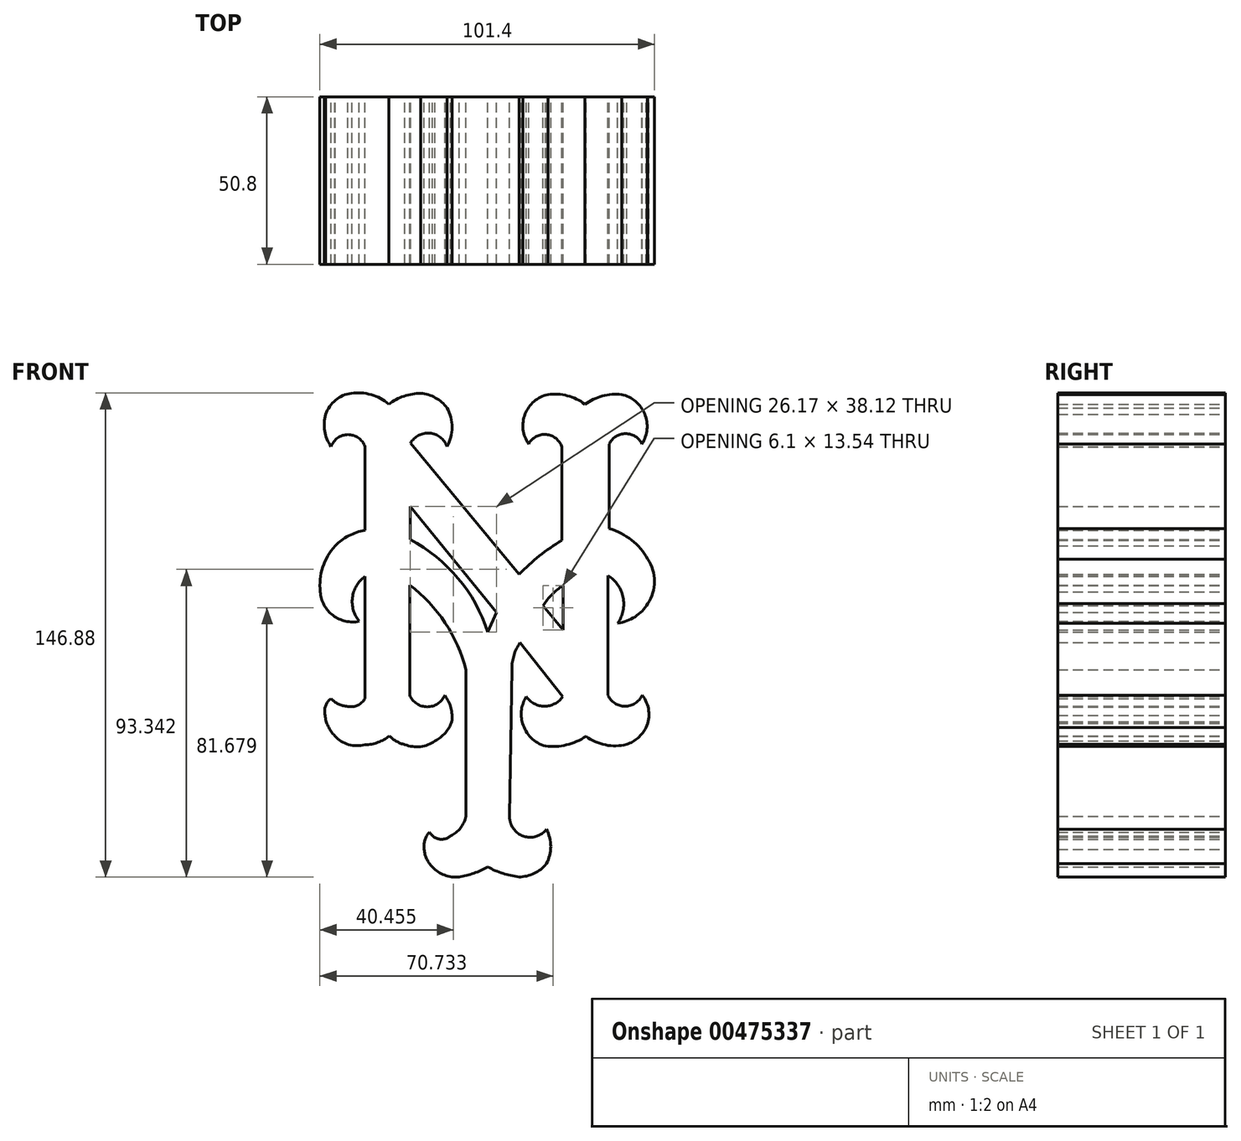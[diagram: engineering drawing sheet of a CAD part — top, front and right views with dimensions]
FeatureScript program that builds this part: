
annotation { "Feature Type Name" : "Feature", "Feature Type Description" : "" }
export const myFeature = defineFeature(function(context is Context, id is Id, definition is map)
    precondition{}
    {
        {
            var Q0;
            Q0=qCreatedBy(makeId("Front.planeOp"),FACE);
            var sketch = newSketch(context, id + "F0", { "sketchPlane" : qUnion([Q0])});
            skLineSegment(sketch, "E0", {"start": v(-23.55, 39.4) * mm, "end": v(-23.55, 29.33) * mm});
            skLineSegment(sketch, "E1", {"start": v(-23.55, 39.4) * mm, "end": v(2.62, 7.32) * mm});
            skLineSegment(sketch, "E2", {"start": v(2.62, 7.32) * mm, "end": v(0, 1.27) * mm});
            skArc(sketch, "E3", {"start": v(0, 1.27) * mm, "mid": v(-9.02, 17.61) * mm, "end": v(-23.55, 29.33) * mm});
            skLineSegment(sketch, "E4", {"start": v(22.87, 15.44) * mm, "end": v(22.87, 1.9) * mm});
            skLineSegment(sketch, "E5", {"start": v(22.87, 1.9) * mm, "end": v(16.76, 9.33) * mm});
            skArc(sketch, "E6", {"start": v(22.87, 15.44) * mm, "mid": v(19.48, 12.72) * mm, "end": v(16.76, 9.33) * mm});
            skLineSegment(sketch, "E7", {"start": v(9.48, 18.87) * mm, "end": v(-23.46, 58.56) * mm});
            skArc(sketch, "E8", {"start": v(22.44, 29.13) * mm, "mid": v(15.64, 24.4) * mm, "end": v(9.48, 18.87) * mm});
            skLineSegment(sketch, "E9", {"start": v(22.44, 29.13) * mm, "end": v(22.44, 57.48) * mm});
            skArc(sketch, "E10", {"start": v(22.44, 57.48) * mm, "mid": v(17.68, 61.21) * mm, "end": v(12.34, 58.37) * mm});
            skArc(sketch, "E11", {"start": v(18.22, 73.36) * mm, "mid": v(11.28, 67.43) * mm, "end": v(12.34, 58.37) * mm});
            skArc(sketch, "E12", {"start": v(29.45, 70.38) * mm, "mid": v(24.13, 72.98) * mm, "end": v(18.22, 73.36) * mm});
            skArc(sketch, "E13", {"start": v(40.58, 73.36) * mm, "mid": v(34.73, 72.92) * mm, "end": v(29.45, 70.38) * mm});
            skArc(sketch, "E14", {"start": v(46.73, 58.37) * mm, "mid": v(47.54, 67.46) * mm, "end": v(40.58, 73.36) * mm});
            skArc(sketch, "E15", {"start": v(46.73, 58.37) * mm, "mid": v(41.78, 61.48) * mm, "end": v(36.83, 58.37) * mm});
            skLineSegment(sketch, "E16", {"start": v(36.83, 58.37) * mm, "end": v(36.83, 32.65) * mm});
            skArc(sketch, "E17", {"start": v(48.5, 23.43) * mm, "mid": v(43.58, 29.2) * mm, "end": v(36.83, 32.65) * mm});
            skArc(sketch, "E18", {"start": v(48.5, 9.92) * mm, "mid": v(50.48, 16.67) * mm, "end": v(48.5, 23.43) * mm});
            skArc(sketch, "E19", {"start": v(39.37, 4) * mm, "mid": v(44.6, 5.93) * mm, "end": v(48.5, 9.92) * mm});
            skArc(sketch, "E20", {"start": v(39.37, 4) * mm, "mid": v(41, 11.85) * mm, "end": v(36.41, 18.42) * mm});
            skLineSegment(sketch, "E21", {"start": v(36.41, 18.42) * mm, "end": v(36.41, -17.86) * mm});
            skArc(sketch, "E22", {"start": v(36.41, -17.86) * mm, "mid": v(41.58, -21.22) * mm, "end": v(46.76, -17.86) * mm});
            skArc(sketch, "E23", {"start": v(48, -27.68) * mm, "mid": v(48.78, -22.6) * mm, "end": v(46.76, -17.86) * mm});
            skArc(sketch, "E24", {"start": v(42.08, -32.77) * mm, "mid": v(45.51, -30.78) * mm, "end": v(48, -27.68) * mm});
            skArc(sketch, "E25", {"start": v(29.76, -30.3) * mm, "mid": v(35.64, -32.92) * mm, "end": v(42.08, -32.77) * mm});
            skArc(sketch, "E26", {"start": v(17.44, -33.27) * mm, "mid": v(23.87, -32.9) * mm, "end": v(29.76, -30.3) * mm});
            skArc(sketch, "E27", {"start": v(10.54, -26.37) * mm, "mid": v(13.07, -30.73) * mm, "end": v(17.44, -33.27) * mm});
            skArc(sketch, "E28", {"start": v(11.69, -18.32) * mm, "mid": v(10.21, -22.21) * mm, "end": v(10.54, -26.37) * mm});
            skArc(sketch, "E29", {"start": v(11.69, -18.32) * mm, "mid": v(17.2, -21.2) * mm, "end": v(22.7, -18.32) * mm});
            skLineSegment(sketch, "E30", {"start": v(22.7, -18.32) * mm, "end": v(9.71, -1.89) * mm});
            skArc(sketch, "E31", {"start": v(9.71, -1.89) * mm, "mid": v(7.92, -5.65) * mm, "end": v(7.25, -9.77) * mm});
            skLineSegment(sketch, "E32", {"start": v(7.25, -9.77) * mm, "end": v(6.56, -54.45) * mm});
            skArc(sketch, "E33", {"start": v(6.56, -54.45) * mm, "mid": v(6.7, -55.93) * mm, "end": v(7.18, -57.33) * mm});
            skArc(sketch, "E34", {"start": v(7.18, -57.33) * mm, "mid": v(12.13, -60.9) * mm, "end": v(17.75, -58.53) * mm});
            skArc(sketch, "E35", {"start": v(17.75, -68.96) * mm, "mid": v(19.07, -63.74) * mm, "end": v(17.75, -58.53) * mm});
            skArc(sketch, "E36", {"start": v(9.42, -72.95) * mm, "mid": v(14.04, -71.9) * mm, "end": v(17.75, -68.96) * mm});
            skArc(sketch, "E37", {"start": v(0, -69.93) * mm, "mid": v(4.56, -71.9) * mm, "end": v(9.42, -72.95) * mm});
            skArc(sketch, "E38", {"start": v(-8.72, -72.95) * mm, "mid": v(-4.22, -71.83) * mm, "end": v(0, -69.93) * mm});
            skArc(sketch, "E39", {"start": v(-16.81, -69.93) * mm, "mid": v(-13.13, -72.4) * mm, "end": v(-8.72, -72.95) * mm});
            skArc(sketch, "E40", {"start": v(-19.3, -64.64) * mm, "mid": v(-18.54, -67.51) * mm, "end": v(-16.81, -69.93) * mm});
            skArc(sketch, "E41", {"start": v(-17.68, -59.36) * mm, "mid": v(-19.11, -61.8) * mm, "end": v(-19.3, -64.64) * mm});
            skArc(sketch, "E42", {"start": v(-17.68, -59.36) * mm, "mid": v(-14.77, -61.48) * mm, "end": v(-11.3, -60.54) * mm});
            skArc(sketch, "E43", {"start": v(-11.3, -60.54) * mm, "mid": v(-8.29, -58.12) * mm, "end": v(-6.67, -54.6) * mm});
            skLineSegment(sketch, "E44", {"start": v(-6.67, -54.6) * mm, "end": v(-6.67, -10.18) * mm});
            skArc(sketch, "E45", {"start": v(-6.67, -10.18) * mm, "mid": v(-12.96, 4.15) * mm, "end": v(-23.68, 15.55) * mm});
            skLineSegment(sketch, "E46", {"start": v(-23.68, 15.55) * mm, "end": v(-23.68, -17.92) * mm});
            skArc(sketch, "E47", {"start": v(-23.68, -17.92) * mm, "mid": v(-18.37, -21.37) * mm, "end": v(-13.06, -17.92) * mm});
            skArc(sketch, "E48", {"start": v(-10.91, -25.85) * mm, "mid": v(-11.2, -21.67) * mm, "end": v(-13.06, -17.92) * mm});
            skArc(sketch, "E49", {"start": v(-16.02, -31.76) * mm, "mid": v(-12.93, -29.27) * mm, "end": v(-10.91, -25.85) * mm});
            skArc(sketch, "E50", {"start": v(-25.16, -32.84) * mm, "mid": v(-20.46, -33.44) * mm, "end": v(-16.02, -31.76) * mm});
            skArc(sketch, "E51", {"start": v(-29.87, -30.15) * mm, "mid": v(-27.71, -31.84) * mm, "end": v(-25.16, -32.84) * mm});
            skArc(sketch, "E52", {"start": v(-37.26, -32.84) * mm, "mid": v(-33.32, -32.16) * mm, "end": v(-29.87, -30.15) * mm});
            skArc(sketch, "E53", {"start": v(-46.4, -30.15) * mm, "mid": v(-42.22, -32.81) * mm, "end": v(-37.26, -32.84) * mm});
            skArc(sketch, "E54", {"start": v(-49.36, -23.97) * mm, "mid": v(-48.43, -27.32) * mm, "end": v(-46.4, -30.15) * mm});
            skArc(sketch, "E55", {"start": v(-47.6, -18.86) * mm, "mid": v(-49.23, -21.16) * mm, "end": v(-49.36, -23.97) * mm});
            skArc(sketch, "E56", {"start": v(-47.6, -18.86) * mm, "mid": v(-45.27, -20.53) * mm, "end": v(-42.5, -21.28) * mm});
            skArc(sketch, "E57", {"start": v(-42.5, -21.28) * mm, "mid": v(-39.49, -20.92) * mm, "end": v(-37.26, -18.86) * mm});
            skLineSegment(sketch, "E58", {"start": v(-37.26, -18.86) * mm, "end": v(-37.26, 18.15) * mm});
            skArc(sketch, "E59", {"start": v(-37.26, 18.15) * mm, "mid": v(-41.08, 11.74) * mm, "end": v(-39, 4.56) * mm});
            skArc(sketch, "E60", {"start": v(-50.81, 13.53) * mm, "mid": v(-46.94, 6.37) * mm, "end": v(-39, 4.56) * mm});
            skArc(sketch, "E61", {"start": v(-37.26, 32.2) * mm, "mid": v(-42.17, 30.52) * mm, "end": v(-46.33, 27.42) * mm});
            skLineSegment(sketch, "E62", {"start": v(-37.26, 32.2) * mm, "end": v(-37.26, 57.6) * mm});
            skArc(sketch, "E63", {"start": v(-37.26, 57.6) * mm, "mid": v(-42.4, 61.19) * mm, "end": v(-47.53, 57.6) * mm});
            skArc(sketch, "E64", {"start": v(-49.17, 67.32) * mm, "mid": v(-49.48, 62.27) * mm, "end": v(-47.53, 57.6) * mm});
            skArc(sketch, "E65", {"start": v(-41.4, 73.74) * mm, "mid": v(-46.2, 71.63) * mm, "end": v(-49.17, 67.32) * mm});
            skArc(sketch, "E66", {"start": v(-30.04, 70.45) * mm, "mid": v(-35.37, 73.3) * mm, "end": v(-41.4, 73.74) * mm});
            skArc(sketch, "E67", {"start": v(-20.33, 73.74) * mm, "mid": v(-25.44, 72.85) * mm, "end": v(-30.04, 70.45) * mm});
            skArc(sketch, "E68", {"start": v(-12.4, 69.26) * mm, "mid": v(-15.89, 72.35) * mm, "end": v(-20.33, 73.74) * mm});
            skArc(sketch, "E69", {"start": v(-12.4, 57.6) * mm, "mid": v(-10.81, 63.43) * mm, "end": v(-12.4, 69.26) * mm});
            skArc(sketch, "E70", {"start": v(-12.4, 57.6) * mm, "mid": v(-17.63, 61.64) * mm, "end": v(-23.46, 58.56) * mm});
            skArc(sketch, "E71", {"start": v(-46.33, 27.42) * mm, "mid": v(-50.06, 20.95) * mm, "end": v(-50.81, 13.53) * mm});
            skSolve(sketch);
        }
        {
            var Q0;
            Q0=makeQuery(id+"F0.imprint","IMPRINT",FACE,{"disambiguationData":[TD([[makeQuery(id+"F0.imprint","IMPRINT",EDGE,{"derivedFrom":sQuery(id+"F0.wireOp",EDGE,"E0")}),-1.0]])]});
            extrude(context, id + "F1", {"entities" : qUnion([Q0]), "depth" : 50.8 * mm});
        }
    });
